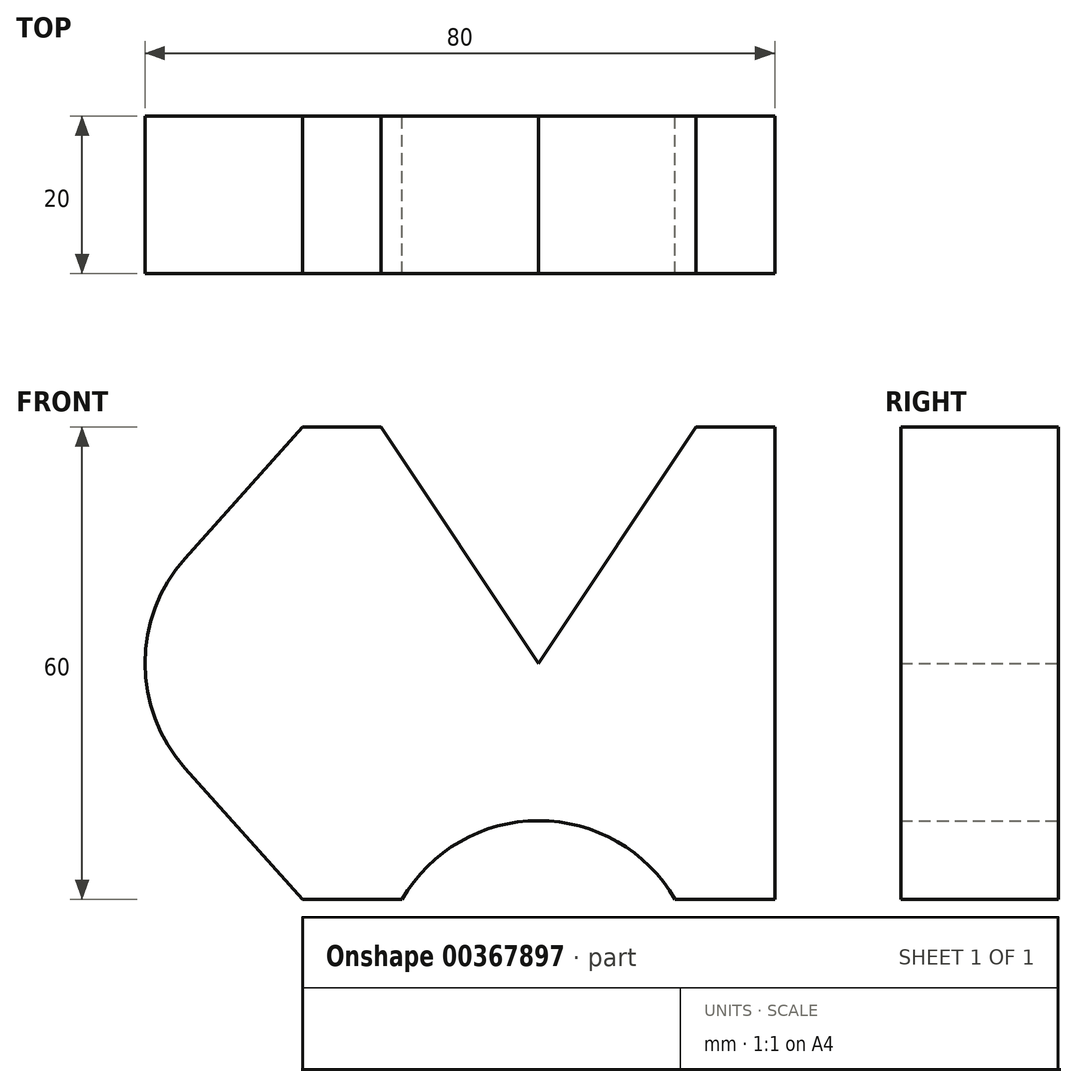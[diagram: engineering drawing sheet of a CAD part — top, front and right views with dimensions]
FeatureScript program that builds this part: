
annotation { "Feature Type Name" : "Feature", "Feature Type Description" : "" }
export const myFeature = defineFeature(function(context is Context, id is Id, definition is map)
    precondition{}
    {
        {
            var Q0;
            Q0=qCreatedBy(makeId("Front.planeOp"),FACE);
            var sketch = newSketch(context, id + "F0", { "sketchPlane" : qUnion([Q0])});
            skLineSegment(sketch, "E0", {"start": v(0, 0) * mm, "end": v(20, 30) * mm});
            skLineSegment(sketch, "E1", {"start": v(20, 30) * mm, "end": v(30, 30) * mm});
            skLineSegment(sketch, "E2", {"start": v(30, 30) * mm, "end": v(30, -30) * mm});
            skLineSegment(sketch, "E3", {"start": v(30, -30) * mm, "end": v(17.32, -30) * mm});
            skArc(sketch, "E4", {"start": v(17.32, -30) * mm, "mid": v(0, -20) * mm, "end": v(-17.32, -30) * mm});
            skLineSegment(sketch, "E5", {"start": v(-17.32, -30) * mm, "end": v(-30, -30) * mm});
            skLineSegment(sketch, "E6", {"start": v(0, 0) * mm, "end": v(-20, 30) * mm});
            skLineSegment(sketch, "E7", {"start": v(-20, 30) * mm, "end": v(-30, 30) * mm});
            skLineSegment(sketch, "E8", {"start": v(-30, 30) * mm, "end": v(-44.9, 13.33) * mm});
            skLineSegment(sketch, "E9", {"start": v(-30, -30) * mm, "end": v(-44.9, -13.33) * mm});
            skArc(sketch, "E10", {"start": v(-44.9, 13.33) * mm, "mid": v(-50, 0) * mm, "end": v(-44.9, -13.33) * mm});
            skLineSegment(sketch, "E11", {"start": v(-30, 30) * mm, "end": v(-30, -30) * mm, "construction": true});
            skSolve(sketch);
        }
        {
            var Q0;
            Q0 = qSketchRegion(id + "F0", true);
            extrude(context, id + "F1", {"entities" : qUnion([Q0]), "depth" : 20 * mm});
        }
    });
